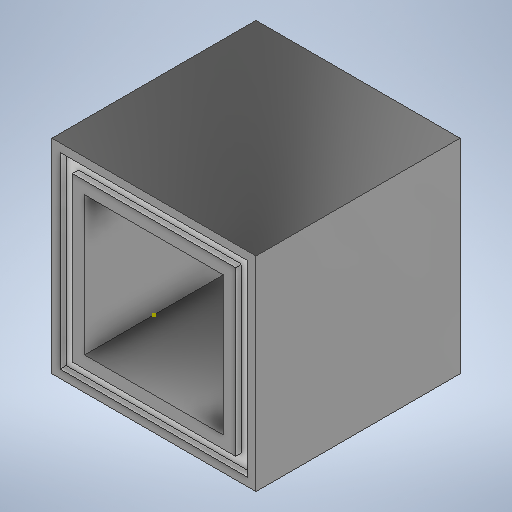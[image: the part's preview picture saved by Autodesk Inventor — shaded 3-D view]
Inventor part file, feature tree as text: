
AUTODESK INVENTOR PART (.ipt)
format: ipt  version: 2025.2 (Build 292293000, 293)  size: 224,768 bytes
history: native  units: mm
features: sketch x5, other x1, extrude x1, sweep x1
ambient origin geometry x8: Origin, YZ Plane, XZ Plane, XY Plane, X Axis, Y Axis, Z Axis, Center Point
bodies: Body1 (feature_tree)
feature tree (8):
  other  "Sólido1"
  extrude  "Extrusão1"  Depth=8.0mm
  sketch  "Esboço2"  dims[d3=50.0mm d4=0.0mm]
  sketch  "Esboço3"  dims[d5=3.5mm]
  sketch  "Esboço8"  dims[d6=3.0mm]
  sweep  "Varredura1"
  sketch  "Esboço1"  dims[d0=50.0mm d2=8.0mm]
  sketch  "Esboço9"  dims[d7=21.5mm d8=0.0mm d9=0.0mm]
